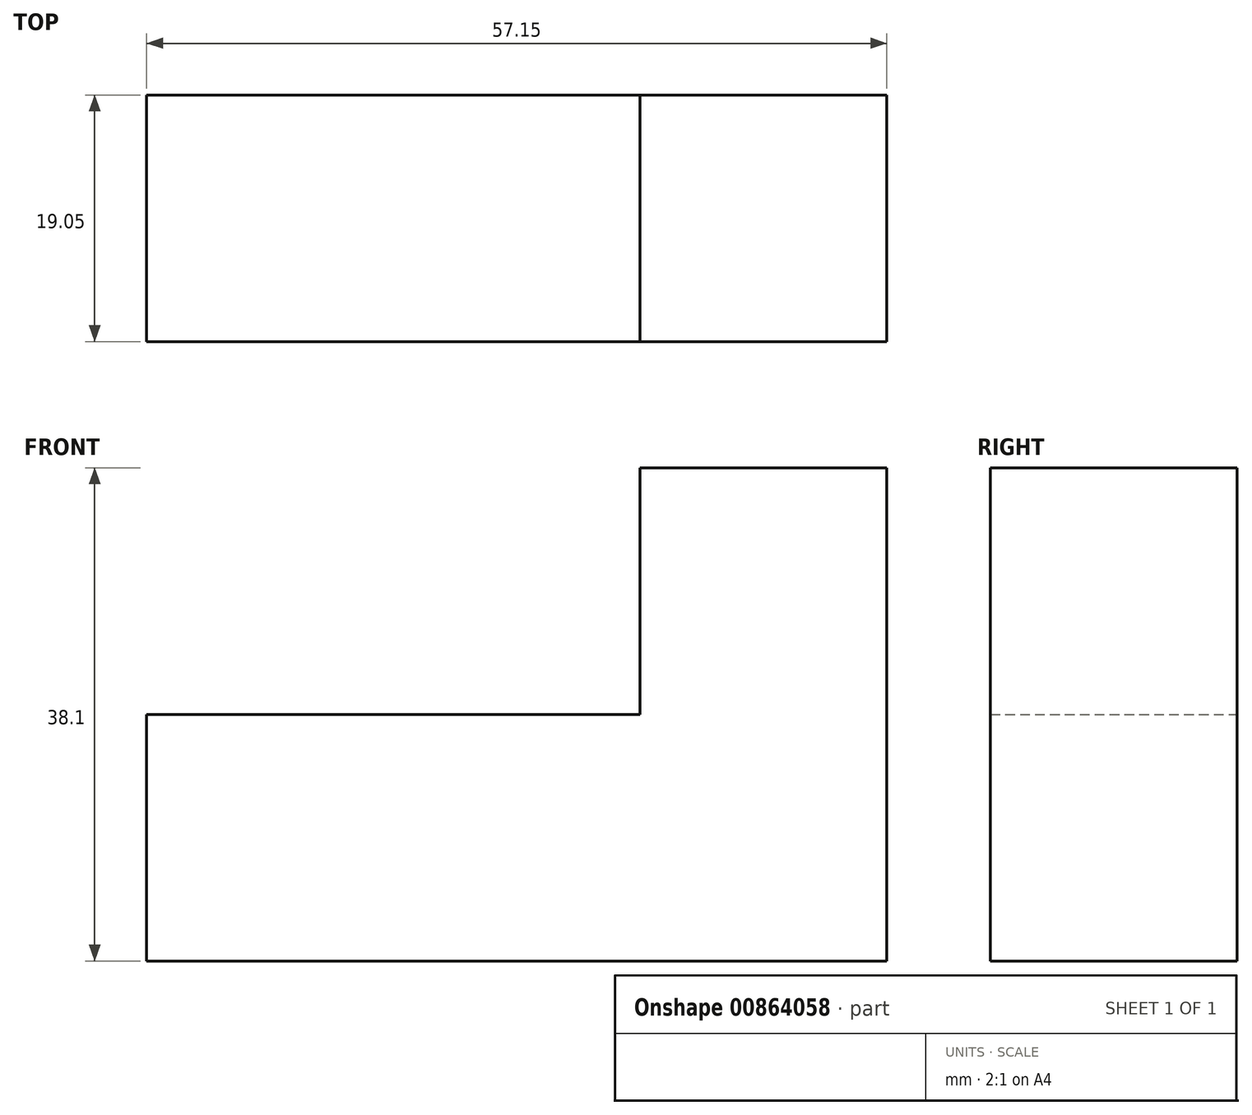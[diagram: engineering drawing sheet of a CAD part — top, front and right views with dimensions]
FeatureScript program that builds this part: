
annotation { "Feature Type Name" : "Feature", "Feature Type Description" : "" }
export const myFeature = defineFeature(function(context is Context, id is Id, definition is map)
    precondition{}
    {
        {
            var Q0;
            Q0=qCreatedBy(makeId("Front.planeOp"),FACE);
            var sketch = newSketch(context, id + "F0", { "sketchPlane" : qUnion([Q0])});
            skLineSegment(sketch, "E0", {"start": v(0, 0) * mm, "end": v(57.15, 0) * mm});
            skLineSegment(sketch, "E1", {"start": v(57.15, 0) * mm, "end": v(57.15, 38.1) * mm});
            skLineSegment(sketch, "E2", {"start": v(57.15, 38.1) * mm, "end": v(38.1, 38.1) * mm});
            skLineSegment(sketch, "E3", {"start": v(38.1, 38.1) * mm, "end": v(38.1, 19.05) * mm});
            skLineSegment(sketch, "E4", {"start": v(38.1, 19.05) * mm, "end": v(0, 19.05) * mm});
            skLineSegment(sketch, "E5", {"start": v(0, 19.05) * mm, "end": v(0, 0) * mm});
            skSolve(sketch);
        }
        {
            var Q0;
            Q0 = qSketchRegion(id + "F0", true);
            extrude(context, id + "F1", {"entities" : qUnion([Q0]), "depth" : 19.05 * mm, "offsetDistance" : 25.4 * mm});
        }
    });
